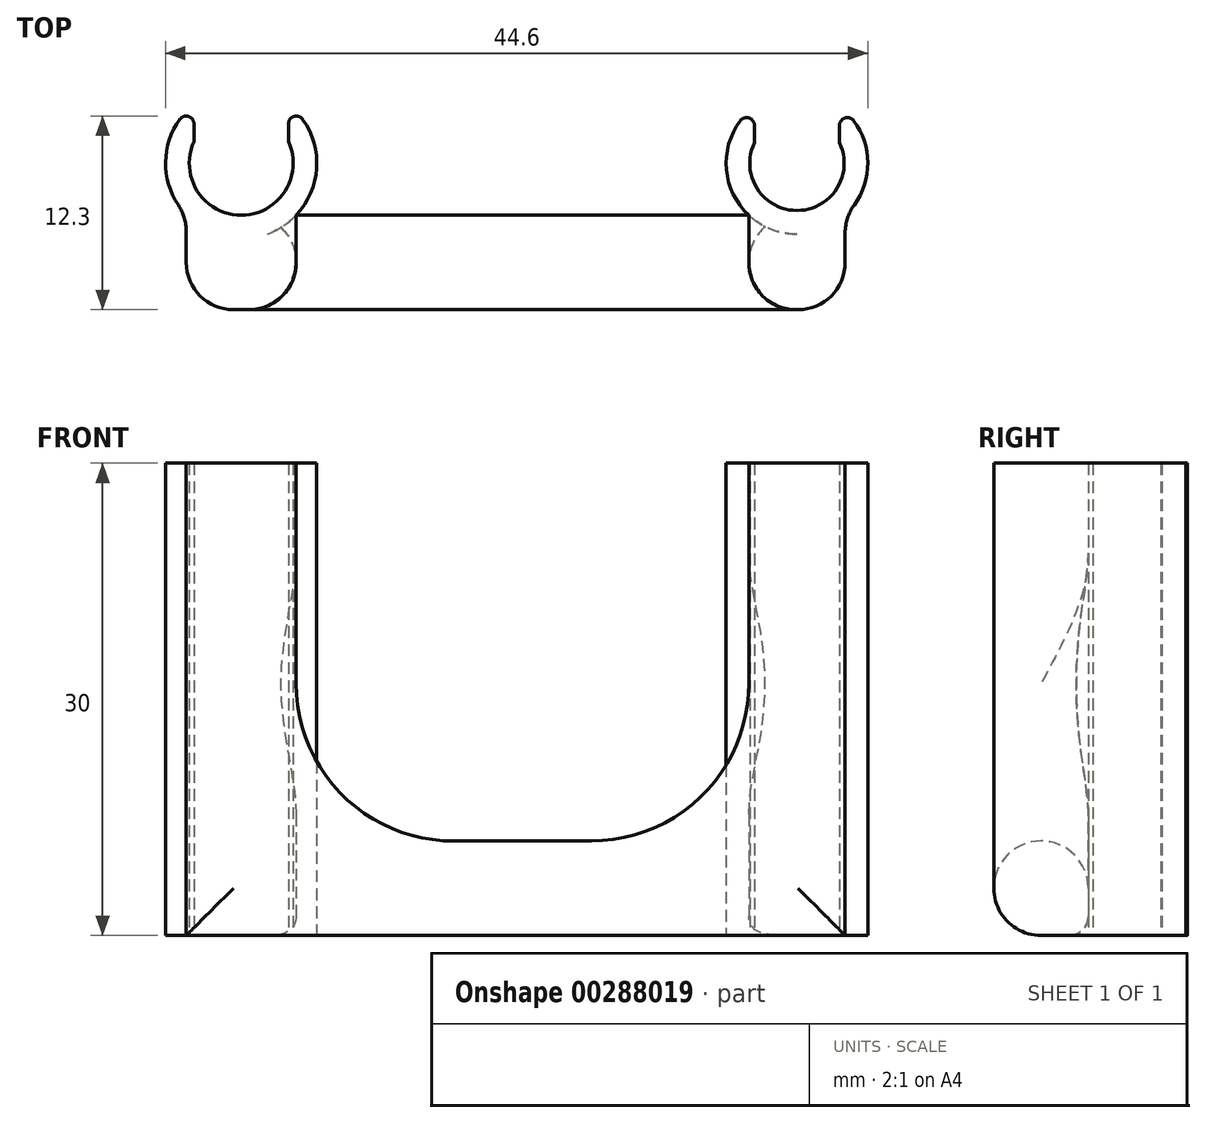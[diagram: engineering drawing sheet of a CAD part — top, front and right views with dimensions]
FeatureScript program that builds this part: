
annotation { "Feature Type Name" : "Feature", "Feature Type Description" : "" }
export const myFeature = defineFeature(function(context is Context, id is Id, definition is map)
    precondition{}
    {
        {
            var Q0;
            Q0=qCreatedBy(makeId("Top.planeOp"),FACE);
            var sketch = newSketch(context, id + "F0", { "sketchPlane" : qUnion([Q0])});
            skArc(sketch, "E0", {"start": v(-19.18, 1.37) * mm, "mid": v(-16.18, -3.3) * mm, "end": v(-13.18, 1.37) * mm});
            skArc(sketch, "E1", {"start": v(16.42, 1.3) * mm, "mid": v(19.12, -3) * mm, "end": v(21.82, 1.3) * mm});
            skLineSegment(sketch, "E2.bottom", {"start": v(-13.18, 0) * mm, "end": v(-19.18, 0) * mm, "construction": true});
            skLineSegment(sketch, "E2.top", {"start": v(-13.18, 6.54) * mm, "end": v(-19.18, 6.54) * mm, "construction": true});
            skLineSegment(sketch, "E2.left", {"start": v(-13.18, 0) * mm, "end": v(-13.18, 2.5) * mm});
            skLineSegment(sketch, "E2.right", {"start": v(-19.18, 0) * mm, "end": v(-19.18, 2.5) * mm});
            skLineSegment(sketch, "E3.bottom", {"start": v(21.82, 0) * mm, "end": v(16.42, 0) * mm, "construction": true});
            skLineSegment(sketch, "E3.top", {"start": v(21.82, 6.54) * mm, "end": v(16.42, 6.54) * mm, "construction": true});
            skLineSegment(sketch, "E3.left", {"start": v(21.82, 0) * mm, "end": v(21.82, 2.4) * mm});
            skLineSegment(sketch, "E3.right", {"start": v(16.42, 0) * mm, "end": v(16.42, 2.4) * mm});
            skArc(sketch, "E4.0", {"start": v(-20.08, 2.79) * mm, "mid": v(-16.18, -4.8) * mm, "end": v(-12.27, 2.79) * mm});
            skArc(sketch, "E5.0", {"start": v(15.52, 2.7) * mm, "mid": v(19.12, -4.5) * mm, "end": v(22.72, 2.7) * mm});
            skPoint(sketch, "E6.firstSnap0", {"position": v(-16.18, -3.3) * mm});
            skLineSegment(sketch, "E6.bottom", {"start": v(-19.66, -3.3) * mm, "end": v(22.18, -3.3) * mm});
            skLineSegment(sketch, "E6.top", {"start": v(-19.66, -9.3) * mm, "end": v(22.18, -9.3) * mm});
            skLineSegment(sketch, "E6.left", {"start": v(-19.66, -3.3) * mm, "end": v(-19.66, -9.3) * mm});
            skLineSegment(sketch, "E6.right", {"start": v(22.18, -3.3) * mm, "end": v(22.18, -9.3) * mm});
            skArc(sketch, "E7.filletArc", {"start": v(-19.18, 2.5) * mm, "mid": v(-19.52, 2.97) * mm, "end": v(-20.08, 2.79) * mm});
            skArc(sketch, "E8.filletArc", {"start": v(-12.27, 2.79) * mm, "mid": v(-12.83, 2.97) * mm, "end": v(-13.18, 2.5) * mm});
            skArc(sketch, "E9.filletArc", {"start": v(16.42, 2.4) * mm, "mid": v(16.08, 2.87) * mm, "end": v(15.52, 2.7) * mm});
            skArc(sketch, "E10.filletArc", {"start": v(22.72, 2.7) * mm, "mid": v(22.16, 2.87) * mm, "end": v(21.82, 2.4) * mm});
            skLineSegment(sketch, "E11", {"start": v(-12.7, -3.3) * mm, "end": v(-12.7, -9.3) * mm});
            skLineSegment(sketch, "E12", {"start": v(16.06, -3.3) * mm, "end": v(16.06, -9.3) * mm});
            skSolve(sketch);
        }
        {
            var Q0;
            {var subQ5=sQuery(id+"F0.wireOp",EDGE,"E7.filletArc");Q0=makeQuery(id+"F0.imprint","IMPRINT",FACE,{"disambiguationData":[TD([[makeQuery(id+"F0.imprint","IMPRINT",EDGE,{"derivedFrom":subQ5}),1.0]])]});}
            var Q1;
            {var subQ0=sQuery(id+"F0.wireOp",EDGE,"E6.bottom");var subQ4=makeQuery(id+"F0.imprint","INTERSECT",VERTEX,{"derivedFrom":[sQuery(id+"F0.wireOp",EDGE,"E0"),subQ0]});Q1=makeQuery(id+"F0.imprint","IMPRINT",FACE,{"disambiguationData":[TD([[makeQuery(id+"F0.imprint","IMPRINT",EDGE,{"disambiguationData":[TD([[subQ4,-1.0]])],"derivedFrom":subQ0}),-1.0]])]});}
            var Q2;
            {var subQ7=sQuery(id+"F0.wireOp",EDGE,"E8.filletArc");Q2=makeQuery(id+"F0.imprint","IMPRINT",FACE,{"disambiguationData":[TD([[makeQuery(id+"F0.imprint","IMPRINT",EDGE,{"derivedFrom":subQ7}),1.0]])]});}
            var Q3;
            {var subQ1=sQuery(id+"F0.wireOp",EDGE,"E1");Q3=makeQuery(id+"F0.imprint","IMPRINT",FACE,{"disambiguationData":[TD([[makeQuery(id+"F0.imprint","IMPRINT",EDGE,{"derivedFrom":subQ1}),-1.0]])]});}
            var Q4;
            {var subQ0=sQuery(id+"F0.wireOp",EDGE,"E6.bottom");var subQ1=sQuery(id+"F0.wireOp",EDGE,"E5.0");var subQ3=makeQuery(id+"F0.imprint","INTERSECT",VERTEX,{"derivedFrom":[subQ1,subQ0]});Q4=makeQuery(id+"F0.imprint","IMPRINT",FACE,{"disambiguationData":[TD([[makeQuery(id+"F0.imprint","IMPRINT",EDGE,{"disambiguationData":[TD([[subQ3,-1.0]])],"derivedFrom":subQ1}),1.0]])]});}
            var Q5;
            {var subQ0=sQuery(id+"F0.wireOp",EDGE,"E6.left");Q5=makeQuery(id+"F0.imprint","IMPRINT",FACE,{"disambiguationData":[TD([[makeQuery(id+"F0.imprint","IMPRINT",EDGE,{"derivedFrom":subQ0}),1.0]])]});}
            var Q6;
            {var subQ0=sQuery(id+"F0.wireOp",EDGE,"E6.right");Q6=makeQuery(id+"F0.imprint","IMPRINT",FACE,{"disambiguationData":[TD([[makeQuery(id+"F0.imprint","IMPRINT",EDGE,{"derivedFrom":subQ0}),-1.0]])]});}
            extrude(context, id + "F1", {"entities" : qUnion([Q0, Q1, Q2, Q3, Q4, Q5, Q6]), "depth" : 30 * mm});
        }
        {
            var Q0;
            Q0=makeQuery(id+"F0.imprint","IMPRINT",FACE,{"disambiguationData":[TD([[makeQuery(id+"F0.imprint","IMPRINT",EDGE,{"derivedFrom":sQuery(id+"F0.wireOp",EDGE,"E6.top")}),1.0]])]});
            extrude(context, id + "F2", {"entities" : qUnion([Q0]), "operationType" : NewBodyOperationType.ADD, "depth" : 6 * mm});
        }
        {
            var Q0;
            Q0=makeQuery(id+"F2.boolean.opBoolean","INTERSECT",EDGE,{"derivedFrom":[makeQuery(id+"F1.opExtrude","SWEPT_FACE",FACE,{"disambiguationData":[OSD([sQuery(id+"F0.wireOp",EDGE,"E12")])]}),makeQuery(id+"F2.opExtrude","CAP_FACE",FACE,{"disambiguationData":[OSD([sQuery(id+"F0.wireOp",EDGE,"E4.0"),sQuery(id+"F0.wireOp",EDGE,"E5.0"),sQuery(id+"F0.wireOp",EDGE,"E6.bottom"),sQuery(id+"F0.wireOp",EDGE,"E6.top"),sQuery(id+"F0.wireOp",EDGE,"E6.left"),sQuery(id+"F0.wireOp",EDGE,"E6.right")])],"isStart":false})]});
            var Q1;
            Q1=makeQuery(id+"F2.boolean.opBoolean","INTERSECT",EDGE,{"derivedFrom":[makeQuery(id+"F1.opExtrude","SWEPT_FACE",FACE,{"disambiguationData":[OSD([sQuery(id+"F0.wireOp",EDGE,"E11")])]}),makeQuery(id+"F2.opExtrude","CAP_FACE",FACE,{"disambiguationData":[OSD([sQuery(id+"F0.wireOp",EDGE,"E4.0"),sQuery(id+"F0.wireOp",EDGE,"E5.0"),sQuery(id+"F0.wireOp",EDGE,"E6.bottom"),sQuery(id+"F0.wireOp",EDGE,"E6.top"),sQuery(id+"F0.wireOp",EDGE,"E6.left"),sQuery(id+"F0.wireOp",EDGE,"E6.right")])],"isStart":false})]});
            fillet(context, id + "F3", {"entities" : qUnion([Q0, Q1]), "radius" : 10 * mm, "tangentPropagation" : true, "allowEdgeOverflow" : false});
        }
        {
            var Q0;
            Q0=makeQuery(id+"F2.opExtrude","CAP_EDGE",EDGE,{"disambiguationData":[OSD([sQuery(id+"F0.wireOp",EDGE,"E6.top")])],"isStart":false});
            var Q1;
            {var subQ0=sQuery(id+"F0.wireOp",EDGE,"E6.top");Q1=makeQuery(id+"F2.boolean.opBoolean","MERGE",EDGE,{"derivedFrom":[makeQuery(id+"F1.opExtrude","CAP_EDGE",EDGE,{"disambiguationData":[OSD([subQ0]),TDD([makeQuery(id+"F0.imprint","IMPRINT",EDGE,{"disambiguationData":[TD([[makeQuery(id+"F0.imprint","INTERSECT",VERTEX,{"derivedFrom":[subQ0,sQuery(id+"F0.wireOp",EDGE,"E6.left")]}),-1.0]])],"derivedFrom":subQ0})])],"isStart":true}),makeQuery(id+"F1.opExtrude","CAP_EDGE",EDGE,{"disambiguationData":[OSD([subQ0]),TDD([makeQuery(id+"F0.imprint","IMPRINT",EDGE,{"disambiguationData":[TD([[makeQuery(id+"F0.imprint","INTERSECT",VERTEX,{"derivedFrom":[subQ0,sQuery(id+"F0.wireOp",EDGE,"E6.right")]}),1.0]])],"derivedFrom":subQ0})])],"isStart":true}),makeQuery(id+"F2.opExtrude","CAP_EDGE",EDGE,{"disambiguationData":[OSD([subQ0])],"isStart":true})]});}
            var Q2;
            Q2=makeQuery(id+"F1.opExtrude","SWEPT_EDGE",EDGE,{"disambiguationData":[OSD([sQuery(id+"F0.wireOp",EDGE,"E6.top"),sQuery(id+"F0.wireOp",EDGE,"E6.left")])]});
            var Q3;
            Q3=makeQuery(id+"F1.opExtrude","SWEPT_EDGE",EDGE,{"disambiguationData":[OSD([sQuery(id+"F0.wireOp",EDGE,"E6.top"),sQuery(id+"F0.wireOp",EDGE,"E6.right")])]});
            var Q4;
            Q4=makeQuery(id+"F1.opExtrude","SWEPT_EDGE",EDGE,{"disambiguationData":[OSD([sQuery(id+"F0.wireOp",EDGE,"E5.0"),sQuery(id+"F0.wireOp",EDGE,"E6.bottom"),sQuery(id+"F0.wireOp",EDGE,"E6.right")])]});
            var Q5;
            Q5=makeQuery(id+"F1.opExtrude","SWEPT_EDGE",EDGE,{"disambiguationData":[OSD([sQuery(id+"F0.wireOp",EDGE,"E4.0"),sQuery(id+"F0.wireOp",EDGE,"E6.bottom"),sQuery(id+"F0.wireOp",EDGE,"E6.left")])]});
            var Q6;
            Q6=makeQuery(id+"F2.opExtrude","CAP_EDGE",EDGE,{"disambiguationData":[OSD([sQuery(id+"F0.wireOp",EDGE,"E6.bottom")])],"isStart":false});
            fillet(context, id + "F4", {"entities" : qUnion([Q0, Q1, Q2, Q3, Q4, Q5, Q6]), "radius" : 3 * mm, "tangentPropagation" : true, "allowEdgeOverflow" : false});
        }
        {
            var Q0;
            Q0=makeQuery(id+"F2.opExtrude","CAP_EDGE",EDGE,{"disambiguationData":[OSD([sQuery(id+"F0.wireOp",EDGE,"E6.bottom")])],"isStart":true});
            fillet(context, id + "F5", {"entities" : qUnion([Q0]), "radius" : 1.2 * mm, "tangentPropagation" : true, "allowEdgeOverflow" : false});
        }
    });
